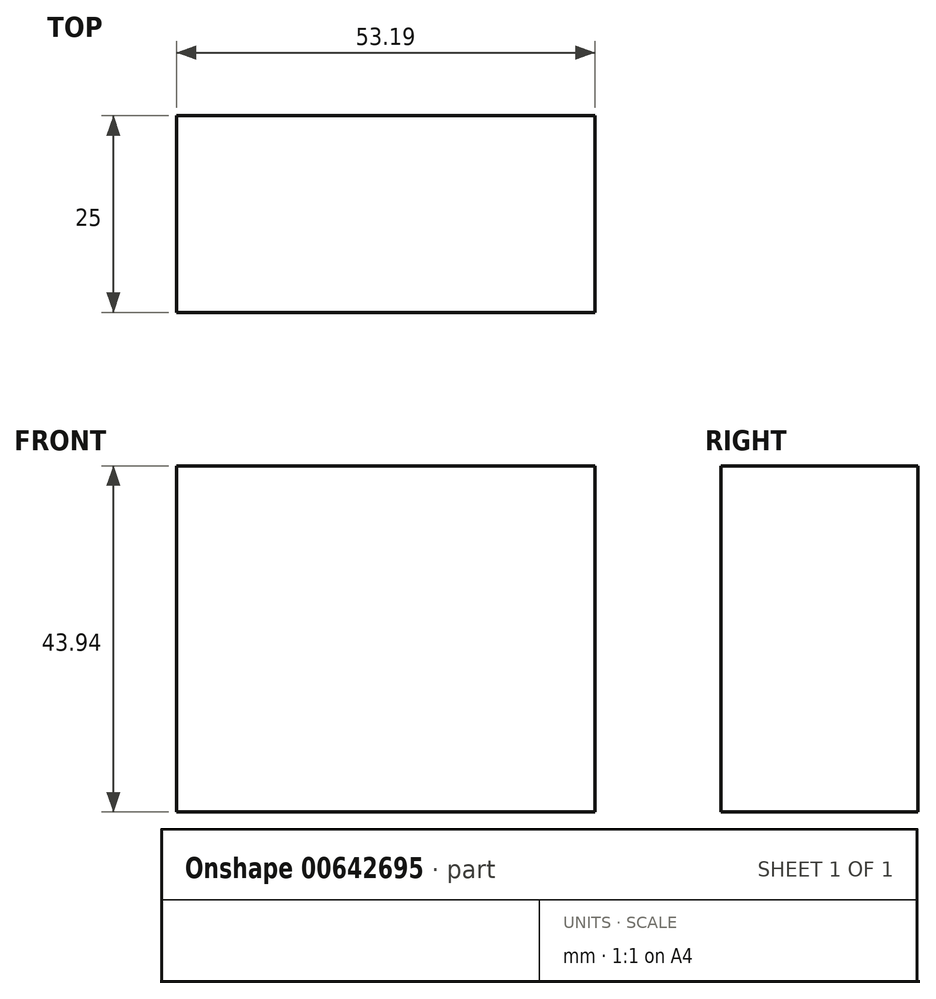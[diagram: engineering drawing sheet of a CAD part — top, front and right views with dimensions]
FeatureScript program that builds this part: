
annotation { "Feature Type Name" : "Feature", "Feature Type Description" : "" }
export const myFeature = defineFeature(function(context is Context, id is Id, definition is map)
    precondition{}
    {
        {
            var Q0;
            Q0=qCreatedBy(makeId("Front.planeOp"),FACE);
            var sketch = newSketch(context, id + "F0", { "sketchPlane" : qUnion([Q0])});
            skLineSegment(sketch, "E0.bottom", {"start": v(-147.57, 23.56) * mm, "end": v(-94.38, 23.56) * mm});
            skLineSegment(sketch, "E0.top", {"start": v(-147.57, 67.5) * mm, "end": v(-94.38, 67.5) * mm});
            skLineSegment(sketch, "E0.left", {"start": v(-147.57, 23.56) * mm, "end": v(-147.57, 67.5) * mm});
            skLineSegment(sketch, "E0.right", {"start": v(-94.38, 23.56) * mm, "end": v(-94.38, 67.5) * mm});
            skPoint(sketch, "E0.middle", {"position": v(-120.98, 45.53) * mm});
            skSolve(sketch);
        }
        {
            var Q0;
            Q0=makeQuery(id+"F0.imprint","IMPRINT",FACE,{"disambiguationData":[TD([[makeQuery(id+"F0.imprint","IMPRINT",EDGE,{"derivedFrom":sQuery(id+"F0.wireOp",EDGE,"E0.bottom")}),1.0]])]});
            extrude(context, id + "F1", {"entities" : qUnion([Q0]), "depth" : 25 * mm, "offsetDistance" : 25 * mm});
        }
    });
